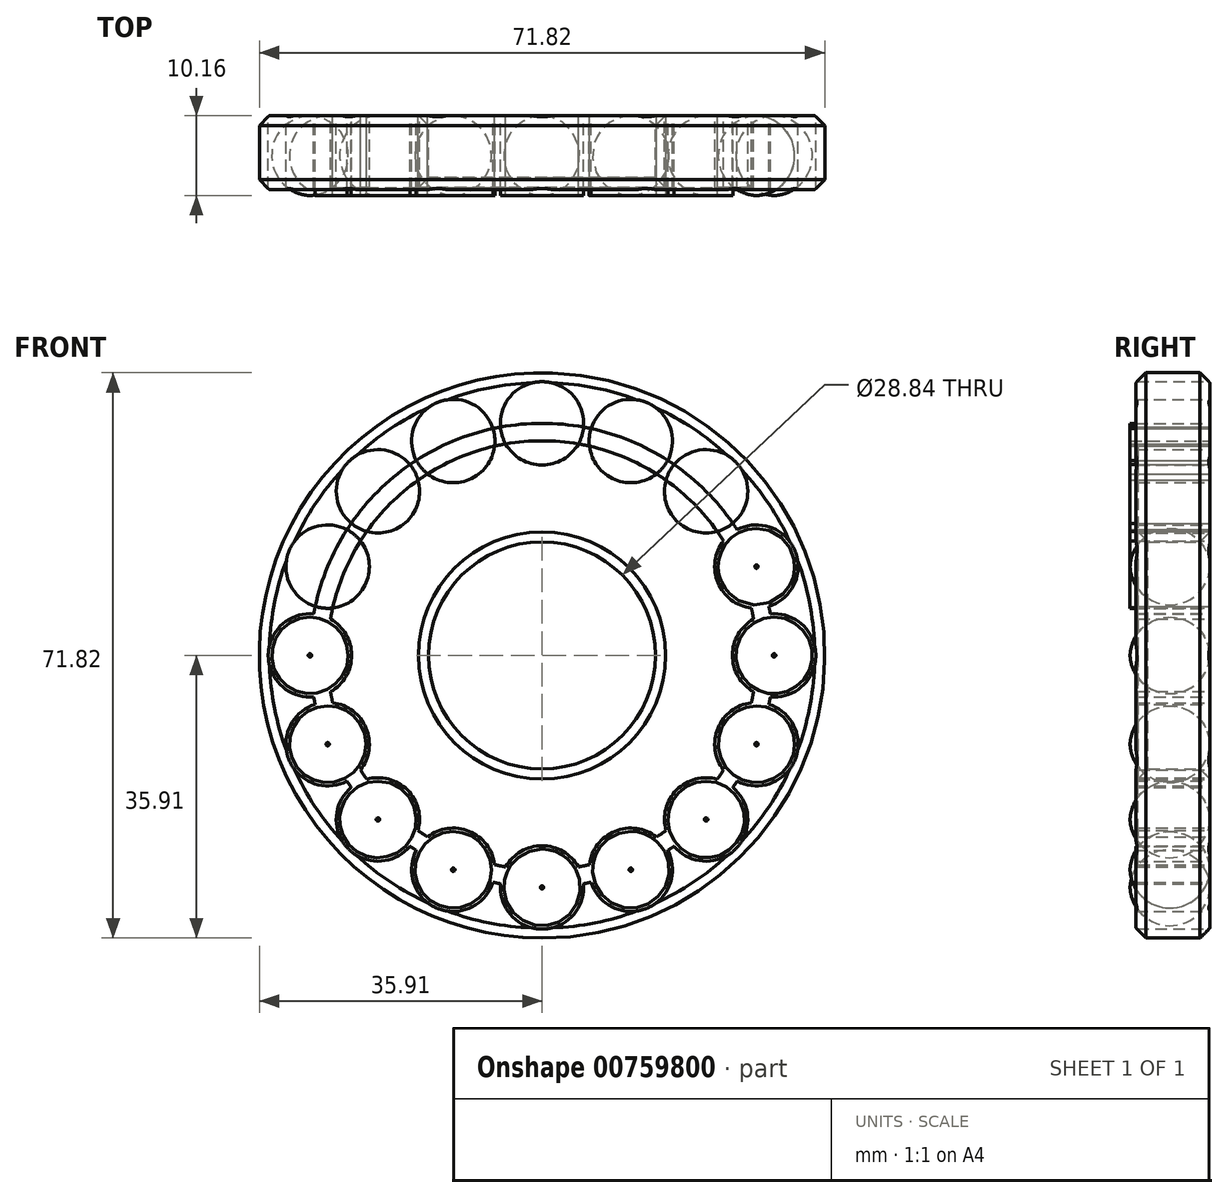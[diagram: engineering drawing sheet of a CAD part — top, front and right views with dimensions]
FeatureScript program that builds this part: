
annotation { "Feature Type Name" : "Feature", "Feature Type Description" : "" }
export const myFeature = defineFeature(function(context is Context, id is Id, definition is map)
    precondition{}
    {
        {
            var Q0;
            Q0=qCreatedBy(makeId("Front.planeOp"),FACE);
            var sketch = newSketch(context, id + "F0", { "sketchPlane" : qUnion([Q0])});
            skCircle(sketch, "E0", {"center": v(0, 0) * mm, "radius": 35.91 * mm});
            skCircle(sketch, "E1", {"center": v(0, 29.48) * mm, "radius": 5.3 * mm});
            skCircle(sketch, "E2.1.0", {"center": v(-11.28, 27.23) * mm, "radius": 5.3 * mm});
            skCircle(sketch, "E2.2.0", {"center": v(-20.84, 20.84) * mm, "radius": 5.3 * mm});
            skCircle(sketch, "E2.3.0", {"center": v(-27.23, 11.28) * mm, "radius": 5.3 * mm});
            skCircle(sketch, "E2.4.0", {"center": v(-29.48, 0) * mm, "radius": 5.3 * mm});
            skCircle(sketch, "E2.5.0", {"center": v(-27.23, -11.28) * mm, "radius": 5.3 * mm});
            skCircle(sketch, "E2.6.0", {"center": v(-20.84, -20.84) * mm, "radius": 5.3 * mm});
            skCircle(sketch, "E2.7.0", {"center": v(-11.28, -27.23) * mm, "radius": 5.3 * mm});
            skCircle(sketch, "E2.8.0", {"center": v(0, -29.48) * mm, "radius": 5.3 * mm});
            skCircle(sketch, "E2.9.0", {"center": v(11.28, -27.23) * mm, "radius": 5.3 * mm});
            skCircle(sketch, "E2.10.0", {"center": v(20.84, -20.84) * mm, "radius": 5.3 * mm});
            skCircle(sketch, "E2.11.0", {"center": v(27.23, -11.28) * mm, "radius": 5.3 * mm});
            skCircle(sketch, "E2.12.0", {"center": v(29.48, 0) * mm, "radius": 5.3 * mm});
            skCircle(sketch, "E2.13.0", {"center": v(27.23, 11.28) * mm, "radius": 5.3 * mm});
            skCircle(sketch, "E2.14.0", {"center": v(20.84, 20.84) * mm, "radius": 5.3 * mm});
            skCircle(sketch, "E2.15.0", {"center": v(11.28, 27.23) * mm, "radius": 5.3 * mm});
            skCircle(sketch, "E3", {"center": v(0, 0) * mm, "radius": 14.42 * mm});
            skCircle(sketch, "E4", {"center": v(0, 0) * mm, "radius": 27.26 * mm});
            skCircle(sketch, "E5", {"center": v(0, 0) * mm, "radius": 29.48 * mm});
            skSolve(sketch);
        }
        {
            var Q0;
            Q0=makeQuery(id+"F0.imprint","IMPRINT",FACE,{"disambiguationData":[TD([[makeQuery(id+"F0.imprint","IMPRINT",EDGE,{"derivedFrom":sQuery(id+"F0.wireOp",EDGE,"E3")}),-1.0]])]});
            extrude(context, id + "F1", {"entities" : qUnion([Q0]), "depth" : 9.14 * mm, "offsetDistance" : 25.4 * mm});
        }
        {
            var Q0;
            Q0 = qSketchRegion(id + "F0", true);
            extrude(context, id + "F2", {"entities" : qUnion([Q0]), "depth" : 9.4 * mm, "offsetDistance" : 25.4 * mm});
        }
        {
            var Q0;
            Q0=makeQuery(id+"F0.imprint","IMPRINT",FACE,{"disambiguationData":[TD([[makeQuery(id+"F0.imprint","IMPRINT",EDGE,{"derivedFrom":sQuery(id+"F0.wireOp",EDGE,"E1")}),1.0]])]});
            var Q1;
            Q1=makeQuery(id+"F0.imprint","IMPRINT",FACE,{"disambiguationData":[TD([[makeQuery(id+"F0.imprint","IMPRINT",EDGE,{"derivedFrom":sQuery(id+"F0.wireOp",EDGE,"E2.2.0")}),1.0]])]});
            var Q2;
            Q2=makeQuery(id+"F0.imprint","IMPRINT",FACE,{"disambiguationData":[TD([[makeQuery(id+"F0.imprint","IMPRINT",EDGE,{"derivedFrom":sQuery(id+"F0.wireOp",EDGE,"E2.3.0")}),1.0]])]});
            var Q3;
            Q3=makeQuery(id+"F0.imprint","IMPRINT",FACE,{"disambiguationData":[TD([[makeQuery(id+"F0.imprint","IMPRINT",EDGE,{"derivedFrom":sQuery(id+"F0.wireOp",EDGE,"E2.4.0")}),1.0]])]});
            var Q4;
            Q4=makeQuery(id+"F0.imprint","IMPRINT",FACE,{"disambiguationData":[TD([[makeQuery(id+"F0.imprint","IMPRINT",EDGE,{"derivedFrom":sQuery(id+"F0.wireOp",EDGE,"E2.5.0")}),1.0]])]});
            var Q5;
            Q5=makeQuery(id+"F0.imprint","IMPRINT",FACE,{"disambiguationData":[TD([[makeQuery(id+"F0.imprint","IMPRINT",EDGE,{"derivedFrom":sQuery(id+"F0.wireOp",EDGE,"E2.6.0")}),1.0]])]});
            var Q6;
            Q6=makeQuery(id+"F0.imprint","IMPRINT",FACE,{"disambiguationData":[TD([[makeQuery(id+"F0.imprint","IMPRINT",EDGE,{"derivedFrom":sQuery(id+"F0.wireOp",EDGE,"E2.1.0")}),1.0]])]});
            var Q7;
            Q7=makeQuery(id+"F0.imprint","IMPRINT",FACE,{"disambiguationData":[TD([[makeQuery(id+"F0.imprint","IMPRINT",EDGE,{"derivedFrom":sQuery(id+"F0.wireOp",EDGE,"E2.7.0")}),1.0]])]});
            var Q8;
            Q8=makeQuery(id+"F0.imprint","IMPRINT",FACE,{"disambiguationData":[TD([[makeQuery(id+"F0.imprint","IMPRINT",EDGE,{"derivedFrom":sQuery(id+"F0.wireOp",EDGE,"E2.8.0")}),1.0]])]});
            var Q9;
            Q9=makeQuery(id+"F0.imprint","IMPRINT",FACE,{"disambiguationData":[TD([[makeQuery(id+"F0.imprint","IMPRINT",EDGE,{"derivedFrom":sQuery(id+"F0.wireOp",EDGE,"E2.9.0")}),1.0]])]});
            var Q10;
            Q10=makeQuery(id+"F0.imprint","IMPRINT",FACE,{"disambiguationData":[TD([[makeQuery(id+"F0.imprint","IMPRINT",EDGE,{"derivedFrom":sQuery(id+"F0.wireOp",EDGE,"E2.10.0")}),1.0]])]});
            var Q11;
            Q11=makeQuery(id+"F0.imprint","IMPRINT",FACE,{"disambiguationData":[TD([[makeQuery(id+"F0.imprint","IMPRINT",EDGE,{"derivedFrom":sQuery(id+"F0.wireOp",EDGE,"E2.11.0")}),1.0]])]});
            var Q12;
            Q12=makeQuery(id+"F0.imprint","IMPRINT",FACE,{"disambiguationData":[TD([[makeQuery(id+"F0.imprint","IMPRINT",EDGE,{"derivedFrom":sQuery(id+"F0.wireOp",EDGE,"E2.12.0")}),1.0]])]});
            var Q13;
            Q13=makeQuery(id+"F0.imprint","IMPRINT",FACE,{"disambiguationData":[TD([[makeQuery(id+"F0.imprint","IMPRINT",EDGE,{"derivedFrom":sQuery(id+"F0.wireOp",EDGE,"E2.13.0")}),1.0]])]});
            var Q14;
            Q14=makeQuery(id+"F0.imprint","IMPRINT",FACE,{"disambiguationData":[TD([[makeQuery(id+"F0.imprint","IMPRINT",EDGE,{"derivedFrom":sQuery(id+"F0.wireOp",EDGE,"E2.14.0")}),1.0]])]});
            var Q15;
            Q15=makeQuery(id+"F0.imprint","IMPRINT",FACE,{"disambiguationData":[TD([[makeQuery(id+"F0.imprint","IMPRINT",EDGE,{"derivedFrom":sQuery(id+"F0.wireOp",EDGE,"E2.15.0")}),1.0]])]});
            var Q16;
            {var subQ0=sQuery(id+"F0.wireOp",EDGE,"E5");var subQ1=sQuery(id+"F0.wireOp",EDGE,"E2.13.0");var subQ2=makeQuery(id+"F0.imprint","INTERSECT",VERTEX,{"disambiguationData":[OD(0.0)],"derivedFrom":[subQ1,subQ0]});Q16=makeQuery(id+"F0.imprint","IMPRINT",FACE,{"disambiguationData":[TD([[makeQuery(id+"F0.imprint","IMPRINT",EDGE,{"disambiguationData":[TD([[subQ2,1.0]])],"derivedFrom":subQ1}),1.0]])]});}
            var Q17;
            {var subQ0=sQuery(id+"F0.wireOp",EDGE,"E5");var subQ1=sQuery(id+"F0.wireOp",EDGE,"E2.14.0");var subQ2=makeQuery(id+"F0.imprint","INTERSECT",VERTEX,{"disambiguationData":[OD(0.0)],"derivedFrom":[subQ1,subQ0]});Q17=makeQuery(id+"F0.imprint","IMPRINT",FACE,{"disambiguationData":[TD([[makeQuery(id+"F0.imprint","IMPRINT",EDGE,{"disambiguationData":[TD([[subQ2,1.0]])],"derivedFrom":subQ1}),1.0]])]});}
            var Q18;
            {var subQ0=sQuery(id+"F0.wireOp",EDGE,"E5");var subQ1=sQuery(id+"F0.wireOp",EDGE,"E2.12.0");var subQ2=makeQuery(id+"F0.imprint","INTERSECT",VERTEX,{"disambiguationData":[OD(0.0)],"derivedFrom":[subQ1,subQ0]});Q18=makeQuery(id+"F0.imprint","IMPRINT",FACE,{"disambiguationData":[TD([[makeQuery(id+"F0.imprint","IMPRINT",EDGE,{"disambiguationData":[TD([[subQ2,1.0]])],"derivedFrom":subQ1}),1.0]])]});}
            var Q19;
            {var subQ0=sQuery(id+"F0.wireOp",EDGE,"E5");var subQ1=sQuery(id+"F0.wireOp",EDGE,"E2.11.0");var subQ2=makeQuery(id+"F0.imprint","INTERSECT",VERTEX,{"disambiguationData":[OD(0.0)],"derivedFrom":[subQ1,subQ0]});Q19=makeQuery(id+"F0.imprint","IMPRINT",FACE,{"disambiguationData":[TD([[makeQuery(id+"F0.imprint","IMPRINT",EDGE,{"disambiguationData":[TD([[subQ2,1.0]])],"derivedFrom":subQ1}),1.0]])]});}
            var Q20;
            {var subQ0=sQuery(id+"F0.wireOp",EDGE,"E5");var subQ1=sQuery(id+"F0.wireOp",EDGE,"E2.10.0");var subQ2=makeQuery(id+"F0.imprint","INTERSECT",VERTEX,{"disambiguationData":[OD(0.0)],"derivedFrom":[subQ1,subQ0]});Q20=makeQuery(id+"F0.imprint","IMPRINT",FACE,{"disambiguationData":[TD([[makeQuery(id+"F0.imprint","IMPRINT",EDGE,{"disambiguationData":[TD([[subQ2,1.0]])],"derivedFrom":subQ1}),1.0]])]});}
            var Q21;
            {var subQ0=sQuery(id+"F0.wireOp",EDGE,"E5");var subQ1=sQuery(id+"F0.wireOp",EDGE,"E2.9.0");var subQ2=makeQuery(id+"F0.imprint","INTERSECT",VERTEX,{"disambiguationData":[OD(0.0)],"derivedFrom":[subQ1,subQ0]});Q21=makeQuery(id+"F0.imprint","IMPRINT",FACE,{"disambiguationData":[TD([[makeQuery(id+"F0.imprint","IMPRINT",EDGE,{"disambiguationData":[TD([[subQ2,1.0]])],"derivedFrom":subQ1}),1.0]])]});}
            var Q22;
            {var subQ0=sQuery(id+"F0.wireOp",EDGE,"E5");var subQ1=sQuery(id+"F0.wireOp",EDGE,"E2.15.0");var subQ2=makeQuery(id+"F0.imprint","INTERSECT",VERTEX,{"disambiguationData":[OD(0.0)],"derivedFrom":[subQ1,subQ0]});Q22=makeQuery(id+"F0.imprint","IMPRINT",FACE,{"disambiguationData":[TD([[makeQuery(id+"F0.imprint","IMPRINT",EDGE,{"disambiguationData":[TD([[subQ2,1.0]])],"derivedFrom":subQ1}),1.0]])]});}
            var Q23;
            {var subQ0=sQuery(id+"F0.wireOp",EDGE,"E5");var subQ1=sQuery(id+"F0.wireOp",EDGE,"E1");var subQ2=makeQuery(id+"F0.imprint","INTERSECT",VERTEX,{"disambiguationData":[OD(0.0)],"derivedFrom":[subQ1,subQ0]});Q23=makeQuery(id+"F0.imprint","IMPRINT",FACE,{"disambiguationData":[TD([[makeQuery(id+"F0.imprint","IMPRINT",EDGE,{"disambiguationData":[TD([[subQ2,1.0]])],"derivedFrom":subQ1}),1.0]])]});}
            var Q24;
            {var subQ0=sQuery(id+"F0.wireOp",EDGE,"E5");var subQ1=sQuery(id+"F0.wireOp",EDGE,"E2.1.0");var subQ2=makeQuery(id+"F0.imprint","INTERSECT",VERTEX,{"disambiguationData":[OD(0.0)],"derivedFrom":[subQ1,subQ0]});Q24=makeQuery(id+"F0.imprint","IMPRINT",FACE,{"disambiguationData":[TD([[makeQuery(id+"F0.imprint","IMPRINT",EDGE,{"disambiguationData":[TD([[subQ2,1.0]])],"derivedFrom":subQ1}),1.0]])]});}
            var Q25;
            {var subQ0=sQuery(id+"F0.wireOp",EDGE,"E5");var subQ1=sQuery(id+"F0.wireOp",EDGE,"E2.2.0");var subQ2=makeQuery(id+"F0.imprint","INTERSECT",VERTEX,{"disambiguationData":[OD(0.0)],"derivedFrom":[subQ1,subQ0]});Q25=makeQuery(id+"F0.imprint","IMPRINT",FACE,{"disambiguationData":[TD([[makeQuery(id+"F0.imprint","IMPRINT",EDGE,{"disambiguationData":[TD([[subQ2,1.0]])],"derivedFrom":subQ1}),1.0]])]});}
            var Q26;
            {var subQ0=sQuery(id+"F0.wireOp",EDGE,"E5");var subQ1=sQuery(id+"F0.wireOp",EDGE,"E2.3.0");var subQ2=makeQuery(id+"F0.imprint","INTERSECT",VERTEX,{"disambiguationData":[OD(0.0)],"derivedFrom":[subQ1,subQ0]});Q26=makeQuery(id+"F0.imprint","IMPRINT",FACE,{"disambiguationData":[TD([[makeQuery(id+"F0.imprint","IMPRINT",EDGE,{"disambiguationData":[TD([[subQ2,1.0]])],"derivedFrom":subQ1}),1.0]])]});}
            var Q27;
            {var subQ0=sQuery(id+"F0.wireOp",EDGE,"E5");var subQ1=sQuery(id+"F0.wireOp",EDGE,"E2.4.0");var subQ2=makeQuery(id+"F0.imprint","INTERSECT",VERTEX,{"disambiguationData":[OD(0.0)],"derivedFrom":[subQ1,subQ0]});Q27=makeQuery(id+"F0.imprint","IMPRINT",FACE,{"disambiguationData":[TD([[makeQuery(id+"F0.imprint","IMPRINT",EDGE,{"disambiguationData":[TD([[subQ2,1.0]])],"derivedFrom":subQ1}),1.0]])]});}
            var Q28;
            {var subQ0=sQuery(id+"F0.wireOp",EDGE,"E5");var subQ1=sQuery(id+"F0.wireOp",EDGE,"E2.5.0");var subQ2=makeQuery(id+"F0.imprint","INTERSECT",VERTEX,{"disambiguationData":[OD(0.0)],"derivedFrom":[subQ1,subQ0]});Q28=makeQuery(id+"F0.imprint","IMPRINT",FACE,{"disambiguationData":[TD([[makeQuery(id+"F0.imprint","IMPRINT",EDGE,{"disambiguationData":[TD([[subQ2,1.0]])],"derivedFrom":subQ1}),1.0]])]});}
            var Q29;
            {var subQ0=sQuery(id+"F0.wireOp",EDGE,"E5");var subQ1=sQuery(id+"F0.wireOp",EDGE,"E2.6.0");var subQ2=makeQuery(id+"F0.imprint","INTERSECT",VERTEX,{"disambiguationData":[OD(0.0)],"derivedFrom":[subQ1,subQ0]});Q29=makeQuery(id+"F0.imprint","IMPRINT",FACE,{"disambiguationData":[TD([[makeQuery(id+"F0.imprint","IMPRINT",EDGE,{"disambiguationData":[TD([[subQ2,1.0]])],"derivedFrom":subQ1}),1.0]])]});}
            var Q30;
            {var subQ0=sQuery(id+"F0.wireOp",EDGE,"E5");var subQ1=sQuery(id+"F0.wireOp",EDGE,"E2.7.0");var subQ2=makeQuery(id+"F0.imprint","INTERSECT",VERTEX,{"disambiguationData":[OD(0.0)],"derivedFrom":[subQ1,subQ0]});Q30=makeQuery(id+"F0.imprint","IMPRINT",FACE,{"disambiguationData":[TD([[makeQuery(id+"F0.imprint","IMPRINT",EDGE,{"disambiguationData":[TD([[subQ2,1.0]])],"derivedFrom":subQ1}),1.0]])]});}
            var Q31;
            {var subQ0=sQuery(id+"F0.wireOp",EDGE,"E5");var subQ1=sQuery(id+"F0.wireOp",EDGE,"E2.8.0");var subQ2=makeQuery(id+"F0.imprint","INTERSECT",VERTEX,{"disambiguationData":[OD(0.0)],"derivedFrom":[subQ1,subQ0]});Q31=makeQuery(id+"F0.imprint","IMPRINT",FACE,{"disambiguationData":[TD([[makeQuery(id+"F0.imprint","IMPRINT",EDGE,{"disambiguationData":[TD([[subQ2,1.0]])],"derivedFrom":subQ1}),1.0]])]});}
            var Q32;
            {var subQ0=sQuery(id+"F0.wireOp",EDGE,"E4");var subQ1=sQuery(id+"F0.wireOp",EDGE,"E2.7.0");var subQ2=makeQuery(id+"F0.imprint","INTERSECT",VERTEX,{"disambiguationData":[OD(0.0)],"derivedFrom":[subQ1,subQ0]});Q32=makeQuery(id+"F0.imprint","IMPRINT",FACE,{"disambiguationData":[TD([[makeQuery(id+"F0.imprint","IMPRINT",EDGE,{"disambiguationData":[TD([[subQ2,-1.0]])],"derivedFrom":subQ1}),1.0]])]});}
            var Q33;
            {var subQ0=sQuery(id+"F0.wireOp",EDGE,"E4");var subQ1=sQuery(id+"F0.wireOp",EDGE,"E2.6.0");var subQ2=makeQuery(id+"F0.imprint","INTERSECT",VERTEX,{"disambiguationData":[OD(0.0)],"derivedFrom":[subQ1,subQ0]});Q33=makeQuery(id+"F0.imprint","IMPRINT",FACE,{"disambiguationData":[TD([[makeQuery(id+"F0.imprint","IMPRINT",EDGE,{"disambiguationData":[TD([[subQ2,-1.0]])],"derivedFrom":subQ1}),1.0]])]});}
            var Q34;
            {var subQ0=sQuery(id+"F0.wireOp",EDGE,"E4");var subQ1=sQuery(id+"F0.wireOp",EDGE,"E2.5.0");var subQ2=makeQuery(id+"F0.imprint","INTERSECT",VERTEX,{"disambiguationData":[OD(0.0)],"derivedFrom":[subQ1,subQ0]});Q34=makeQuery(id+"F0.imprint","IMPRINT",FACE,{"disambiguationData":[TD([[makeQuery(id+"F0.imprint","IMPRINT",EDGE,{"disambiguationData":[TD([[subQ2,-1.0]])],"derivedFrom":subQ1}),1.0]])]});}
            var Q35;
            {var subQ0=sQuery(id+"F0.wireOp",EDGE,"E4");var subQ1=sQuery(id+"F0.wireOp",EDGE,"E2.4.0");var subQ2=makeQuery(id+"F0.imprint","INTERSECT",VERTEX,{"disambiguationData":[OD(0.0)],"derivedFrom":[subQ1,subQ0]});Q35=makeQuery(id+"F0.imprint","IMPRINT",FACE,{"disambiguationData":[TD([[makeQuery(id+"F0.imprint","IMPRINT",EDGE,{"disambiguationData":[TD([[subQ2,-1.0]])],"derivedFrom":subQ1}),1.0]])]});}
            var Q36;
            {var subQ0=sQuery(id+"F0.wireOp",EDGE,"E4");var subQ1=sQuery(id+"F0.wireOp",EDGE,"E2.3.0");var subQ2=makeQuery(id+"F0.imprint","INTERSECT",VERTEX,{"disambiguationData":[OD(0.0)],"derivedFrom":[subQ1,subQ0]});Q36=makeQuery(id+"F0.imprint","IMPRINT",FACE,{"disambiguationData":[TD([[makeQuery(id+"F0.imprint","IMPRINT",EDGE,{"disambiguationData":[TD([[subQ2,-1.0]])],"derivedFrom":subQ1}),1.0]])]});}
            var Q37;
            {var subQ0=sQuery(id+"F0.wireOp",EDGE,"E4");var subQ1=sQuery(id+"F0.wireOp",EDGE,"E2.2.0");var subQ2=makeQuery(id+"F0.imprint","INTERSECT",VERTEX,{"disambiguationData":[OD(0.0)],"derivedFrom":[subQ1,subQ0]});Q37=makeQuery(id+"F0.imprint","IMPRINT",FACE,{"disambiguationData":[TD([[makeQuery(id+"F0.imprint","IMPRINT",EDGE,{"disambiguationData":[TD([[subQ2,-1.0]])],"derivedFrom":subQ1}),1.0]])]});}
            var Q38;
            {var subQ0=sQuery(id+"F0.wireOp",EDGE,"E4");var subQ1=sQuery(id+"F0.wireOp",EDGE,"E2.1.0");var subQ2=makeQuery(id+"F0.imprint","INTERSECT",VERTEX,{"disambiguationData":[OD(0.0)],"derivedFrom":[subQ1,subQ0]});Q38=makeQuery(id+"F0.imprint","IMPRINT",FACE,{"disambiguationData":[TD([[makeQuery(id+"F0.imprint","IMPRINT",EDGE,{"disambiguationData":[TD([[subQ2,-1.0]])],"derivedFrom":subQ1}),1.0]])]});}
            var Q39;
            {var subQ0=sQuery(id+"F0.wireOp",EDGE,"E4");var subQ1=sQuery(id+"F0.wireOp",EDGE,"E1");var subQ2=makeQuery(id+"F0.imprint","INTERSECT",VERTEX,{"disambiguationData":[OD(0.0)],"derivedFrom":[subQ1,subQ0]});Q39=makeQuery(id+"F0.imprint","IMPRINT",FACE,{"disambiguationData":[TD([[makeQuery(id+"F0.imprint","IMPRINT",EDGE,{"disambiguationData":[TD([[subQ2,-1.0]])],"derivedFrom":subQ1}),1.0]])]});}
            var Q40;
            {var subQ0=sQuery(id+"F0.wireOp",EDGE,"E4");var subQ1=sQuery(id+"F0.wireOp",EDGE,"E2.15.0");var subQ2=makeQuery(id+"F0.imprint","INTERSECT",VERTEX,{"disambiguationData":[OD(0.0)],"derivedFrom":[subQ1,subQ0]});Q40=makeQuery(id+"F0.imprint","IMPRINT",FACE,{"disambiguationData":[TD([[makeQuery(id+"F0.imprint","IMPRINT",EDGE,{"disambiguationData":[TD([[subQ2,-1.0]])],"derivedFrom":subQ1}),1.0]])]});}
            var Q41;
            {var subQ0=sQuery(id+"F0.wireOp",EDGE,"E4");var subQ1=sQuery(id+"F0.wireOp",EDGE,"E2.14.0");var subQ2=makeQuery(id+"F0.imprint","INTERSECT",VERTEX,{"disambiguationData":[OD(0.0)],"derivedFrom":[subQ1,subQ0]});Q41=makeQuery(id+"F0.imprint","IMPRINT",FACE,{"disambiguationData":[TD([[makeQuery(id+"F0.imprint","IMPRINT",EDGE,{"disambiguationData":[TD([[subQ2,-1.0]])],"derivedFrom":subQ1}),1.0]])]});}
            var Q42;
            {var subQ0=sQuery(id+"F0.wireOp",EDGE,"E4");var subQ1=sQuery(id+"F0.wireOp",EDGE,"E2.13.0");var subQ2=makeQuery(id+"F0.imprint","INTERSECT",VERTEX,{"disambiguationData":[OD(0.0)],"derivedFrom":[subQ1,subQ0]});Q42=makeQuery(id+"F0.imprint","IMPRINT",FACE,{"disambiguationData":[TD([[makeQuery(id+"F0.imprint","IMPRINT",EDGE,{"disambiguationData":[TD([[subQ2,-1.0]])],"derivedFrom":subQ1}),1.0]])]});}
            var Q43;
            {var subQ0=sQuery(id+"F0.wireOp",EDGE,"E4");var subQ1=sQuery(id+"F0.wireOp",EDGE,"E2.12.0");var subQ2=makeQuery(id+"F0.imprint","INTERSECT",VERTEX,{"disambiguationData":[OD(0.0)],"derivedFrom":[subQ1,subQ0]});Q43=makeQuery(id+"F0.imprint","IMPRINT",FACE,{"disambiguationData":[TD([[makeQuery(id+"F0.imprint","IMPRINT",EDGE,{"disambiguationData":[TD([[subQ2,-1.0]])],"derivedFrom":subQ1}),1.0]])]});}
            var Q44;
            {var subQ0=sQuery(id+"F0.wireOp",EDGE,"E4");var subQ1=sQuery(id+"F0.wireOp",EDGE,"E2.11.0");var subQ2=makeQuery(id+"F0.imprint","INTERSECT",VERTEX,{"disambiguationData":[OD(0.0)],"derivedFrom":[subQ1,subQ0]});Q44=makeQuery(id+"F0.imprint","IMPRINT",FACE,{"disambiguationData":[TD([[makeQuery(id+"F0.imprint","IMPRINT",EDGE,{"disambiguationData":[TD([[subQ2,-1.0]])],"derivedFrom":subQ1}),1.0]])]});}
            var Q45;
            {var subQ0=sQuery(id+"F0.wireOp",EDGE,"E4");var subQ1=sQuery(id+"F0.wireOp",EDGE,"E2.10.0");var subQ2=makeQuery(id+"F0.imprint","INTERSECT",VERTEX,{"disambiguationData":[OD(0.0)],"derivedFrom":[subQ1,subQ0]});Q45=makeQuery(id+"F0.imprint","IMPRINT",FACE,{"disambiguationData":[TD([[makeQuery(id+"F0.imprint","IMPRINT",EDGE,{"disambiguationData":[TD([[subQ2,-1.0]])],"derivedFrom":subQ1}),1.0]])]});}
            var Q46;
            {var subQ0=sQuery(id+"F0.wireOp",EDGE,"E4");var subQ1=sQuery(id+"F0.wireOp",EDGE,"E2.9.0");var subQ2=makeQuery(id+"F0.imprint","INTERSECT",VERTEX,{"disambiguationData":[OD(0.0)],"derivedFrom":[subQ1,subQ0]});Q46=makeQuery(id+"F0.imprint","IMPRINT",FACE,{"disambiguationData":[TD([[makeQuery(id+"F0.imprint","IMPRINT",EDGE,{"disambiguationData":[TD([[subQ2,-1.0]])],"derivedFrom":subQ1}),1.0]])]});}
            var Q47;
            {var subQ0=sQuery(id+"F0.wireOp",EDGE,"E4");var subQ1=sQuery(id+"F0.wireOp",EDGE,"E2.8.0");var subQ2=makeQuery(id+"F0.imprint","INTERSECT",VERTEX,{"disambiguationData":[OD(0.0)],"derivedFrom":[subQ1,subQ0]});Q47=makeQuery(id+"F0.imprint","IMPRINT",FACE,{"disambiguationData":[TD([[makeQuery(id+"F0.imprint","IMPRINT",EDGE,{"disambiguationData":[TD([[subQ2,-1.0]])],"derivedFrom":subQ1}),1.0]])]});}
            extrude(context, id + "F3", {"entities" : qUnion([Q0, Q1, Q2, Q3, Q4, Q5, Q6, Q7, Q8, Q9, Q10, Q11, Q12, Q13, Q14, Q15, Q16, Q17, Q18, Q19, Q20, Q21, Q22, Q23, Q24, Q25, Q26, Q27, Q28, Q29, Q30, Q31, Q32, Q33, Q34, Q35, Q36, Q37, Q38, Q39, Q40, Q41, Q42, Q43, Q44, Q45, Q46, Q47]), "depth" : 10.16 * mm, "offsetDistance" : 25.4 * mm});
        }
        {
            var Q0;
            Q0=makeQuery(id+"F3.opExtrude","CAP_FACE",FACE,{"disambiguationData":[OSD([sQuery(id+"F0.wireOp",EDGE,"E1")])],"isStart":true});
            var Q1;
            Q1=makeQuery(id+"F3.opExtrude","CAP_FACE",FACE,{"disambiguationData":[OSD([sQuery(id+"F0.wireOp",EDGE,"E2.1.0")])],"isStart":true});
            var Q2;
            Q2=makeQuery(id+"F3.opExtrude","CAP_FACE",FACE,{"disambiguationData":[OSD([sQuery(id+"F0.wireOp",EDGE,"E2.2.0")])],"isStart":true});
            var Q3;
            Q3=makeQuery(id+"F3.opExtrude","CAP_FACE",FACE,{"disambiguationData":[OSD([sQuery(id+"F0.wireOp",EDGE,"E2.3.0")])],"isStart":true});
            var Q4;
            Q4=makeQuery(id+"F3.opExtrude","CAP_FACE",FACE,{"disambiguationData":[OSD([sQuery(id+"F0.wireOp",EDGE,"E2.4.0")])],"isStart":true});
            var Q5;
            Q5=makeQuery(id+"F3.opExtrude","CAP_FACE",FACE,{"disambiguationData":[OSD([sQuery(id+"F0.wireOp",EDGE,"E2.5.0")])],"isStart":true});
            var Q6;
            Q6=makeQuery(id+"F3.opExtrude","CAP_FACE",FACE,{"disambiguationData":[OSD([sQuery(id+"F0.wireOp",EDGE,"E2.6.0")])],"isStart":true});
            var Q7;
            Q7=makeQuery(id+"F3.opExtrude","CAP_FACE",FACE,{"disambiguationData":[OSD([sQuery(id+"F0.wireOp",EDGE,"E2.7.0")])],"isStart":true});
            var Q8;
            Q8=makeQuery(id+"F3.opExtrude","CAP_FACE",FACE,{"disambiguationData":[OSD([sQuery(id+"F0.wireOp",EDGE,"E2.8.0")])],"isStart":true});
            var Q9;
            Q9=makeQuery(id+"F3.opExtrude","CAP_FACE",FACE,{"disambiguationData":[OSD([sQuery(id+"F0.wireOp",EDGE,"E2.9.0")])],"isStart":true});
            var Q10;
            Q10=makeQuery(id+"F3.opExtrude","CAP_FACE",FACE,{"disambiguationData":[OSD([sQuery(id+"F0.wireOp",EDGE,"E2.10.0")])],"isStart":true});
            var Q11;
            Q11=makeQuery(id+"F3.opExtrude","CAP_FACE",FACE,{"disambiguationData":[OSD([sQuery(id+"F0.wireOp",EDGE,"E2.11.0")])],"isStart":true});
            var Q12;
            Q12=makeQuery(id+"F3.opExtrude","CAP_FACE",FACE,{"disambiguationData":[OSD([sQuery(id+"F0.wireOp",EDGE,"E2.12.0")])],"isStart":true});
            var Q13;
            Q13=makeQuery(id+"F3.opExtrude","CAP_FACE",FACE,{"disambiguationData":[OSD([sQuery(id+"F0.wireOp",EDGE,"E2.13.0")])],"isStart":true});
            var Q14;
            Q14=makeQuery(id+"F3.opExtrude","CAP_FACE",FACE,{"disambiguationData":[OSD([sQuery(id+"F0.wireOp",EDGE,"E2.14.0")])],"isStart":true});
            var Q15;
            Q15=makeQuery(id+"F3.opExtrude","CAP_FACE",FACE,{"disambiguationData":[OSD([sQuery(id+"F0.wireOp",EDGE,"E2.15.0")])],"isStart":true});
            fillet(context, id + "F4", {"entities" : qUnion([Q0, Q1, Q2, Q3, Q4, Q5, Q6, Q7, Q8, Q9, Q10, Q11, Q12, Q13, Q14, Q15]), "radius" : 5.08 * mm, "tangentPropagation" : true, "allowEdgeOverflow" : false});
        }
        {
            var Q0;
            Q0=makeQuery(id+"F3.opExtrude","CAP_FACE",FACE,{"disambiguationData":[OSD([sQuery(id+"F0.wireOp",EDGE,"E2.2.0")])],"isStart":false});
            var Q1;
            Q1=makeQuery(id+"F3.opExtrude","CAP_FACE",FACE,{"disambiguationData":[OSD([sQuery(id+"F0.wireOp",EDGE,"E2.1.0")])],"isStart":false});
            var Q2;
            Q2=makeQuery(id+"F3.opExtrude","CAP_FACE",FACE,{"disambiguationData":[OSD([sQuery(id+"F0.wireOp",EDGE,"E1")])],"isStart":false});
            var Q3;
            Q3=makeQuery(id+"F3.opExtrude","CAP_FACE",FACE,{"disambiguationData":[OSD([sQuery(id+"F0.wireOp",EDGE,"E2.15.0")])],"isStart":false});
            var Q4;
            Q4=makeQuery(id+"F3.opExtrude","CAP_FACE",FACE,{"disambiguationData":[OSD([sQuery(id+"F0.wireOp",EDGE,"E2.14.0")])],"isStart":false});
            var Q5;
            Q5=makeQuery(id+"F3.opExtrude","CAP_FACE",FACE,{"disambiguationData":[OSD([sQuery(id+"F0.wireOp",EDGE,"E2.13.0")])],"isStart":false});
            var Q6;
            Q6=makeQuery(id+"F3.opExtrude","CAP_FACE",FACE,{"disambiguationData":[OSD([sQuery(id+"F0.wireOp",EDGE,"E2.12.0")])],"isStart":false});
            var Q7;
            Q7=makeQuery(id+"F3.opExtrude","CAP_FACE",FACE,{"disambiguationData":[OSD([sQuery(id+"F0.wireOp",EDGE,"E2.11.0")])],"isStart":false});
            var Q8;
            Q8=makeQuery(id+"F3.opExtrude","CAP_FACE",FACE,{"disambiguationData":[OSD([sQuery(id+"F0.wireOp",EDGE,"E2.10.0")])],"isStart":false});
            var Q9;
            Q9=makeQuery(id+"F3.opExtrude","CAP_FACE",FACE,{"disambiguationData":[OSD([sQuery(id+"F0.wireOp",EDGE,"E2.9.0")])],"isStart":false});
            var Q10;
            Q10=makeQuery(id+"F3.opExtrude","CAP_FACE",FACE,{"disambiguationData":[OSD([sQuery(id+"F0.wireOp",EDGE,"E2.8.0")])],"isStart":false});
            var Q11;
            Q11=makeQuery(id+"F3.opExtrude","CAP_FACE",FACE,{"disambiguationData":[OSD([sQuery(id+"F0.wireOp",EDGE,"E2.7.0")])],"isStart":false});
            var Q12;
            Q12=makeQuery(id+"F3.opExtrude","CAP_FACE",FACE,{"disambiguationData":[OSD([sQuery(id+"F0.wireOp",EDGE,"E2.6.0")])],"isStart":false});
            var Q13;
            Q13=makeQuery(id+"F3.opExtrude","CAP_FACE",FACE,{"disambiguationData":[OSD([sQuery(id+"F0.wireOp",EDGE,"E2.5.0")])],"isStart":false});
            var Q14;
            Q14=makeQuery(id+"F3.opExtrude","CAP_FACE",FACE,{"disambiguationData":[OSD([sQuery(id+"F0.wireOp",EDGE,"E2.4.0")])],"isStart":false});
            var Q15;
            Q15=makeQuery(id+"F3.opExtrude","CAP_FACE",FACE,{"disambiguationData":[OSD([sQuery(id+"F0.wireOp",EDGE,"E2.3.0")])],"isStart":false});
            fillet(context, id + "F5", {"entities" : qUnion([Q0, Q1, Q2, Q3, Q4, Q5, Q6, Q7, Q8, Q9, Q10, Q11, Q12, Q13, Q14, Q15]), "radius" : 5.08 * mm, "tangentPropagation" : true, "allowEdgeOverflow" : false});
        }
        {
            var Q0;
            Q0=makeQuery(id+"F2.opExtrude","CAP_EDGE",EDGE,{"disambiguationData":[OSD([sQuery(id+"F0.wireOp",EDGE,"E0")])],"isStart":false});
            chamfer(context, id + "F6", {"entities" : qUnion([Q0]), "width" : 1.27 * mm, "tangentPropagation" : true});
        }
        {
            var Q0;
            Q0=makeQuery(id+"F2.opExtrude","CAP_EDGE",EDGE,{"disambiguationData":[OSD([sQuery(id+"F0.wireOp",EDGE,"E0")])],"isStart":true});
            chamfer(context, id + "F7", {"entities" : qUnion([Q0]), "width" : 1.27 * mm, "tangentPropagation" : true});
        }
        {
            var Q0;
            Q0=makeQuery(id+"F1.opExtrude","CAP_EDGE",EDGE,{"disambiguationData":[OSD([sQuery(id+"F0.wireOp",EDGE,"E3")])],"isStart":true});
            chamfer(context, id + "F8", {"entities" : qUnion([Q0]), "width" : 1.27 * mm, "tangentPropagation" : true});
        }
        {
            var Q0;
            Q0=makeQuery(id+"F1.opExtrude","CAP_EDGE",EDGE,{"disambiguationData":[OSD([sQuery(id+"F0.wireOp",EDGE,"E3")])],"isStart":false});
            chamfer(context, id + "F9", {"entities" : qUnion([Q0]), "width" : 1.27 * mm, "tangentPropagation" : true});
        }
    });
